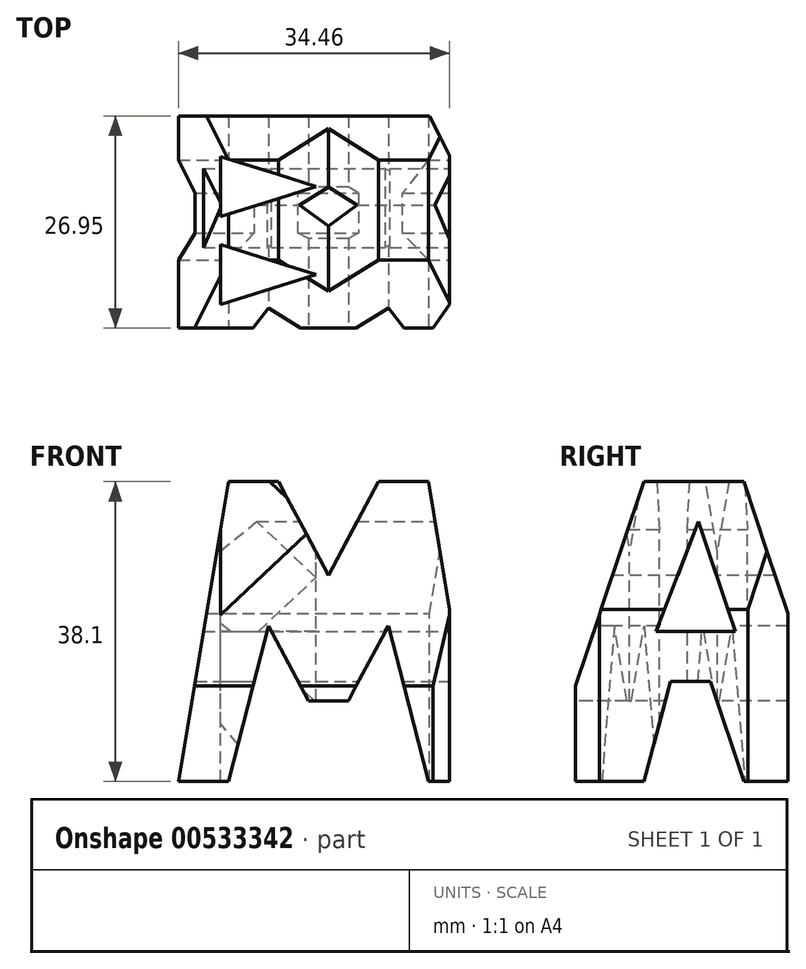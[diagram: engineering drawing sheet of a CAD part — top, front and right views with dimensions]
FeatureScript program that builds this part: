
annotation { "Feature Type Name" : "Feature", "Feature Type Description" : "" }
export const myFeature = defineFeature(function(context is Context, id is Id, definition is map)
    precondition{}
    {
        {
            var Q0;
            Q0=qCreatedBy(makeId("Front.planeOp"),FACE);
            var sketch = newSketch(context, id + "F0", { "sketchPlane" : qUnion([Q0])});
            skLineSegment(sketch, "E0.bottom", {"start": v(0, 0) * mm, "end": v(38.1, 0) * mm});
            skLineSegment(sketch, "E0.top", {"start": v(0, 38.1) * mm, "end": v(38.1, 38.1) * mm});
            skLineSegment(sketch, "E0.left", {"start": v(0, 0) * mm, "end": v(0, 38.1) * mm});
            skLineSegment(sketch, "E0.right", {"start": v(38.1, 0) * mm, "end": v(38.1, 38.1) * mm});
            skSolve(sketch);
        }
        {
            var Q0;
            Q0=makeQuery(id+"F0.imprint","IMPRINT",FACE,{"disambiguationData":[TD([[makeQuery(id+"F0.imprint","IMPRINT",EDGE,{"derivedFrom":sQuery(id+"F0.wireOp",EDGE,"E0.bottom")}),1.0]])]});
            extrude(context, id + "F1", {"entities" : qUnion([Q0]), "depth" : 38.1 * mm, "offsetDistance" : 25.4 * mm});
        }
        {
            var Q0;
            Q0=qCreatedBy(makeId("Front.planeOp"),FACE);
            cPlane(context, id + "F2", {"entities" : qUnion([Q0]), "cplaneType" : CPlaneType.OFFSET, "offset" : 38.1 * mm, "width" : 152.4 * mm, "height" : 152.4 * mm});
        }
        {
            var Q0;
            Q0=qCreatedBy(makeId("Right.planeOp"),FACE);
            cPlane(context, id + "F3", {"entities" : qUnion([Q0]), "cplaneType" : CPlaneType.OFFSET, "offset" : 38.1 * mm, "width" : 152.4 * mm, "height" : 152.4 * mm});
        }
        {
            var Q0;
            Q0=qCreatedBy(makeId("Top.planeOp"),FACE);
            cPlane(context, id + "F4", {"entities" : qUnion([Q0]), "cplaneType" : CPlaneType.OFFSET, "offset" : 38.1 * mm, "width" : 152.4 * mm, "height" : 152.4 * mm});
        }
        {
            var Q0;
            Q0=qCreatedBy(id+"F3.planeOp",FACE);
            var sketch = newSketch(context, id + "F5", { "sketchPlane" : qUnion([Q0])});
            skLineSegment(sketch, "E1", {"start": v(0, 0) * mm, "end": v(0, 38.1) * mm});
            skLineSegment(sketch, "E2", {"start": v(0, 38.1) * mm, "end": v(-38.1, 38.1) * mm});
            skLineSegment(sketch, "E3", {"start": v(-38.1, 38.1) * mm, "end": v(-38.1, 0) * mm});
            skLineSegment(sketch, "E4", {"start": v(-38.1, 0) * mm, "end": v(0, 0) * mm});
            skLineSegment(sketch, "E5", {"start": v(-38.1, 0) * mm, "end": v(-25.4, 38.1) * mm});
            skLineSegment(sketch, "E6", {"start": v(0, 0) * mm, "end": v(-12.7, 38.1) * mm});
            skLineSegment(sketch, "E7", {"start": v(-25.4, 0) * mm, "end": v(-22.01, 12.7) * mm});
            skLineSegment(sketch, "E8", {"start": v(-12.7, 0) * mm, "end": v(-16.93, 12.7) * mm});
            skLineSegment(sketch, "E9", {"start": v(-22.01, 12.7) * mm, "end": v(-16.93, 12.7) * mm});
            skLineSegment(sketch, "E10", {"start": v(-23.83, 19.05) * mm, "end": v(-13.78, 19.05) * mm});
            skLineSegment(sketch, "E11", {"start": v(-13.78, 19.05) * mm, "end": v(-18.44, 33.02) * mm});
            skLineSegment(sketch, "E12", {"start": v(-23.83, 19.05) * mm, "end": v(-18.44, 33.02) * mm});
            skLineSegment(sketch, "E13", {"start": v(-38.1, 38.1) * mm, "end": v(-25.4, 38.1) * mm});
            skSolve(sketch);
        }
        {
            var Q0;
            Q0=makeQuery(id+"F5.imprint","IMPRINT",FACE,{"disambiguationData":[TD([[makeQuery(id+"F5.imprint","IMPRINT",EDGE,{"derivedFrom":sQuery(id+"F5.wireOp",EDGE,"E3")}),1.0]])]});
            var Q1;
            {var subQ0=sQuery(id+"F5.wireOp",EDGE,"E1");Q1=makeQuery(id+"F5.imprint","IMPRINT",FACE,{"disambiguationData":[TD([[makeQuery(id+"F5.imprint","IMPRINT",EDGE,{"derivedFrom":subQ0}),1.0]])]});}
            var Q2;
            Q2=makeQuery(id+"F5.imprint","IMPRINT",FACE,{"disambiguationData":[TD([[makeQuery(id+"F5.imprint","IMPRINT",EDGE,{"derivedFrom":sQuery(id+"F5.wireOp",EDGE,"E10")}),1.0]])]});
            var Q3;
            {var subQ0=sQuery(id+"F5.wireOp",EDGE,"E7");Q3=makeQuery(id+"F5.imprint","IMPRINT",FACE,{"disambiguationData":[TD([[makeQuery(id+"F5.imprint","IMPRINT",EDGE,{"derivedFrom":subQ0}),-1.0]])]});}
            extrude(context, id + "F6", {"entities" : qUnion([Q0, Q1, Q2, Q3]), "operationType" : NewBodyOperationType.REMOVE, "oppositeDirection" : true, "depth" : 38.1 * mm, "offsetDistance" : 25.4 * mm});
        }
        {
            var Q0;
            Q0=qCreatedBy(id+"F2.planeOp",FACE);
            var sketch = newSketch(context, id + "F7", { "sketchPlane" : qUnion([Q0])});
            skLineSegment(sketch, "E14", {"start": v(0, 0) * mm, "end": v(0, 38.1) * mm});
            skLineSegment(sketch, "E15", {"start": v(0, 0) * mm, "end": v(38.1, 0) * mm});
            skLineSegment(sketch, "E16", {"start": v(38.1, 0) * mm, "end": v(38.1, 38.1) * mm});
            skLineSegment(sketch, "E17", {"start": v(38.1, 38.1) * mm, "end": v(0, 38.1) * mm});
            skLineSegment(sketch, "E18", {"start": v(0, 0) * mm, "end": v(6.35, 38.1) * mm});
            skLineSegment(sketch, "E19", {"start": v(38.1, 0) * mm, "end": v(31.75, 38.1) * mm});
            skLineSegment(sketch, "E20", {"start": v(19.05, 26.18) * mm, "end": v(12.7, 38.1) * mm});
            skPoint(sketch, "E20.startSnap0", {"position": v(19.05, 38.1) * mm});
            skLineSegment(sketch, "E21", {"start": v(19.05, 26.18) * mm, "end": v(25.4, 38.1) * mm});
            skLineSegment(sketch, "E22", {"start": v(6.35, 0) * mm, "end": v(11.43, 19.8) * mm});
            skLineSegment(sketch, "E23", {"start": v(11.43, 19.8) * mm, "end": v(16.51, 10.25) * mm});
            skLineSegment(sketch, "E24", {"start": v(16.51, 10.25) * mm, "end": v(21.59, 10.25) * mm});
            skLineSegment(sketch, "E25", {"start": v(21.59, 10.25) * mm, "end": v(26.67, 19.8) * mm});
            skLineSegment(sketch, "E26", {"start": v(26.67, 19.8) * mm, "end": v(31.75, 0) * mm});
            skSolve(sketch);
        }
        {
            var Q0;
            {var subQ0=sQuery(id+"F7.wireOp",EDGE,"E20");Q0=makeQuery(id+"F7.imprint","IMPRINT",FACE,{"disambiguationData":[TD([[makeQuery(id+"F7.imprint","IMPRINT",EDGE,{"derivedFrom":subQ0}),-1.0]])]});}
            var Q1;
            {var subQ0=sQuery(id+"F7.wireOp",EDGE,"E14");Q1=makeQuery(id+"F7.imprint","IMPRINT",FACE,{"disambiguationData":[TD([[makeQuery(id+"F7.imprint","IMPRINT",EDGE,{"derivedFrom":subQ0}),-1.0]])]});}
            var Q2;
            {var subQ0=sQuery(id+"F7.wireOp",EDGE,"E22");Q2=makeQuery(id+"F7.imprint","IMPRINT",FACE,{"disambiguationData":[TD([[makeQuery(id+"F7.imprint","IMPRINT",EDGE,{"derivedFrom":subQ0}),-1.0]])]});}
            var Q3;
            {var subQ0=sQuery(id+"F7.wireOp",EDGE,"E16");Q3=makeQuery(id+"F7.imprint","IMPRINT",FACE,{"disambiguationData":[TD([[makeQuery(id+"F7.imprint","IMPRINT",EDGE,{"derivedFrom":subQ0}),1.0]])]});}
            extrude(context, id + "F8", {"entities" : qUnion([Q0, Q1, Q2, Q3]), "operationType" : NewBodyOperationType.REMOVE, "oppositeDirection" : true, "depth" : 38.1 * mm, "offsetDistance" : 25.4 * mm});
        }
        {
            var Q0;
            Q0=qCreatedBy(id+"F4.planeOp",FACE);
            var sketch = newSketch(context, id + "F9", { "sketchPlane" : qUnion([Q0])});
            skLineSegment(sketch, "E27.bottom", {"start": v(0, 0) * mm, "end": v(38.1, 0) * mm});
            skLineSegment(sketch, "E27.top", {"start": v(0, -38.2) * mm, "end": v(38.1, -38.2) * mm});
            skLineSegment(sketch, "E27.left", {"start": v(0, 0) * mm, "end": v(0, -38.2) * mm});
            skLineSegment(sketch, "E27.right", {"start": v(38.1, 0) * mm, "end": v(38.1, -38.2) * mm});
            skLineSegment(sketch, "E28", {"start": v(0, -7.1) * mm, "end": v(31.88, -7.1) * mm});
            skLineSegment(sketch, "E29", {"start": v(31.88, -7.1) * mm, "end": v(34.46, -12.15) * mm});
            skLineSegment(sketch, "E30", {"start": v(34.46, -12.15) * mm, "end": v(34.46, -31.05) * mm});
            skLineSegment(sketch, "E31", {"start": v(34.46, -31.05) * mm, "end": v(32.37, -34.06) * mm});
            skLineSegment(sketch, "E32", {"start": v(32.37, -34.06) * mm, "end": v(0, -34.06) * mm});
            skLineSegment(sketch, "E33", {"start": v(5.34, -12.26) * mm, "end": v(5.34, -19.88) * mm});
            skLineSegment(sketch, "E34", {"start": v(5.34, -12.26) * mm, "end": v(17.45, -16.07) * mm});
            skLineSegment(sketch, "E35", {"start": v(17.45, -16.07) * mm, "end": v(5.34, -19.88) * mm});
            skLineSegment(sketch, "E36", {"start": v(5.34, -23.43) * mm, "end": v(5.34, -31.05) * mm});
            skLineSegment(sketch, "E37", {"start": v(5.34, -31.05) * mm, "end": v(17.45, -27.24) * mm});
            skLineSegment(sketch, "E38", {"start": v(5.34, -23.43) * mm, "end": v(17.45, -27.24) * mm});
            skSolve(sketch);
        }
        {
            var Q0;
            Q0=makeQuery(id+"F9.imprint","IMPRINT",FACE,{"disambiguationData":[TD([[makeQuery(id+"F9.imprint","IMPRINT",EDGE,{"derivedFrom":sQuery(id+"F9.wireOp",EDGE,"E33")}),1.0]])]});
            var Q1;
            Q1=makeQuery(id+"F9.imprint","IMPRINT",FACE,{"disambiguationData":[TD([[makeQuery(id+"F9.imprint","IMPRINT",EDGE,{"derivedFrom":sQuery(id+"F9.wireOp",EDGE,"E36")}),1.0]])]});
            var Q2;
            {var subQ3=sQuery(id+"F9.wireOp",EDGE,"E27.bottom");Q2=makeQuery(id+"F9.imprint","IMPRINT",FACE,{"disambiguationData":[TD([[makeQuery(id+"F9.imprint","IMPRINT",EDGE,{"derivedFrom":subQ3}),-1.0]])]});}
            extrude(context, id + "F10", {"entities" : qUnion([Q0, Q1, Q2]), "operationType" : NewBodyOperationType.REMOVE, "oppositeDirection" : true, "depth" : 38.1 * mm, "offsetDistance" : 25.4 * mm});
        }
    });
